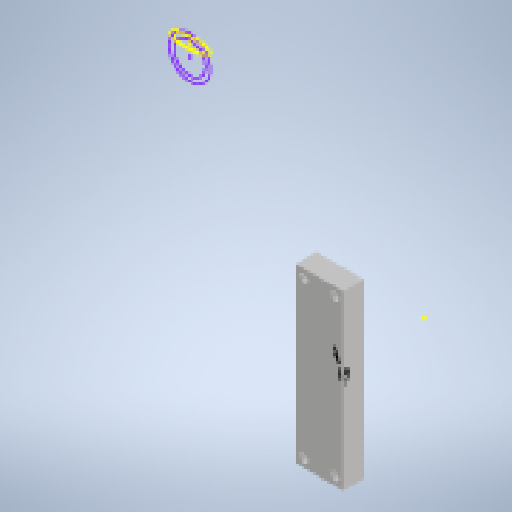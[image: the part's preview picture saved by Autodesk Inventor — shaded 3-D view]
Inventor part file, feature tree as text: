
AUTODESK INVENTOR PART (.ipt)
format: ipt  version: 2024 (Build 280153000, 153)  size: 169,984 bytes
history: native  units: mm
features: other x3, plane x3, extrude x3, sketch x3
ambient origin geometry x8: Origin, YZ Plane, XZ Plane, XY Plane, X Axis, Y Axis, Z Axis, Center Point
bodies: Body1 (feature_tree)
feature tree (12):
  other  "Sólido1"
  plane  "Plano de trabajo2"
  plane  "Plano de trabajo5"
  extrude  "Extrusión5"  Depth=75.0mm
  plane  "Plano de trabajo4"
  extrude  "Extrusión6"  TaperAngle=0.0deg  [1 undecoded]
  extrude  "Extrusión7"  Depth=23.0mm
  sketch  "Boceto7"  dims[d18=15.0mm d19=75.0mm]
  sketch  "Boceto10"  dims[d20=10.0mm d21=0.0mm d28=0.0mm]
  sketch  "Boceto11"  dims[d30=8.0mm d31=0.0mm d32=23.0mm d33=83.0mm d35=7.5mm d36=4.044mm d37=4.044mm d38=20.0mm d39=40.0mm d40=0.0mm]
  other  "ENSAMBLAJE_VENTOSA_2.iam"
  other  "VENTOSA_B:2"
note: 1 required parameter value undecoded (feature->parameter linkage not recoverable at this tier; creation-order binding heuristic only, values carry confidence <= 0.55)
